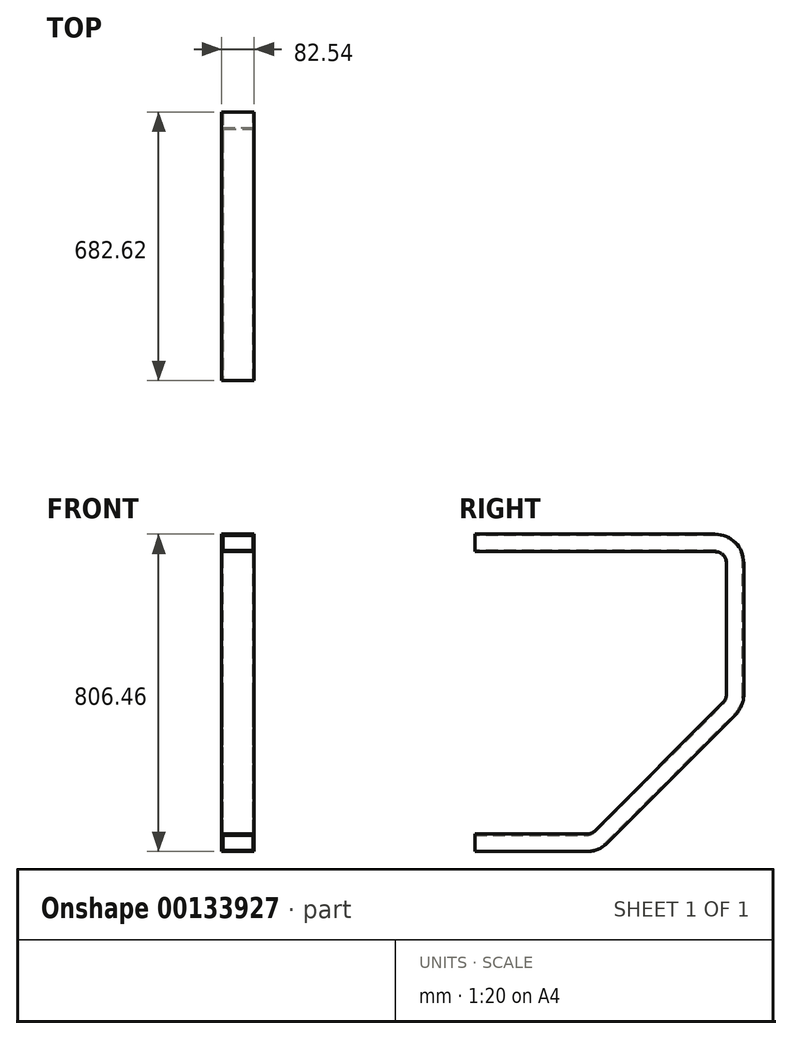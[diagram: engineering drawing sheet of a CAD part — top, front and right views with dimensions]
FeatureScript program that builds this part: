
annotation { "Feature Type Name" : "Feature", "Feature Type Description" : "" }
export const myFeature = defineFeature(function(context is Context, id is Id, definition is map)
    precondition{}
    {
        {
            var Q0;
            Q0=qCreatedBy(makeId("Right.planeOp"),FACE);
            var sketch = newSketch(context, id + "F0", { "sketchPlane" : qUnion([Q0])});
            skLineSegment(sketch, "E0", {"start": v(0, 0) * mm, "end": v(283.76, 0) * mm});
            skLineSegment(sketch, "E1", {"start": v(319.68, 14.88) * mm, "end": v(645.52, 340.72) * mm});
            skLineSegment(sketch, "E2", {"start": v(660.4, 376.64) * mm, "end": v(660.4, 711.2) * mm});
            skLineSegment(sketch, "E3", {"start": v(609.6, 762) * mm, "end": v(0, 762) * mm});
            skPoint(sketch, "E4.visualSharp", {"position": v(304.8, 0) * mm});
            skArc(sketch, "E4.filletArc", {"start": v(283.76, 0) * mm, "mid": v(303.2, 3.87) * mm, "end": v(319.68, 14.88) * mm});
            skPoint(sketch, "E5.visualSharp", {"position": v(660.4, 355.6) * mm});
            skArc(sketch, "E5.filletArc", {"start": v(645.52, 340.72) * mm, "mid": v(656.53, 357.2) * mm, "end": v(660.4, 376.64) * mm});
            skPoint(sketch, "E6.visualSharp", {"position": v(660.4, 762) * mm});
            skArc(sketch, "E6.filletArc", {"start": v(660.4, 711.2) * mm, "mid": v(645.52, 747.12) * mm, "end": v(609.6, 762) * mm});
            skSolve(sketch);
        }
        {
            var Q0;
            Q0=qCreatedBy(makeId("Front.planeOp"),FACE);
            var sketch = newSketch(context, id + "F1", { "sketchPlane" : qUnion([Q0])});
            skLineSegment(sketch, "E7.bottom", {"start": v(38.1, 19.05) * mm, "end": v(-38.1, 19.05) * mm});
            skLineSegment(sketch, "E7.top", {"start": v(38.1, -19.05) * mm, "end": v(-38.1, -19.05) * mm});
            skLineSegment(sketch, "E7.left", {"start": v(38.1, 19.05) * mm, "end": v(38.1, -19.05) * mm});
            skLineSegment(sketch, "E7.right", {"start": v(-38.1, 19.05) * mm, "end": v(-38.1, -19.05) * mm});
            skPoint(sketch, "E7.middle", {"position": v(0, 0) * mm});
            skLineSegment(sketch, "E8.0", {"start": v(41.28, 22.22) * mm, "end": v(-41.28, 22.22) * mm});
            skLineSegment(sketch, "E8.1", {"start": v(41.28, 22.22) * mm, "end": v(41.28, -22.23) * mm});
            skLineSegment(sketch, "E8.2", {"start": v(41.28, -22.23) * mm, "end": v(-41.28, -22.23) * mm});
            skLineSegment(sketch, "E8.3", {"start": v(-41.28, 22.22) * mm, "end": v(-41.28, -22.23) * mm});
            skSolve(sketch);
        }
        {
            var Q0;
            Q0=makeQuery(id+"F1.imprint","IMPRINT",FACE,{"disambiguationData":[TD([[makeQuery(id+"F1.imprint","IMPRINT",EDGE,{"derivedFrom":sQuery(id+"F1.wireOp",EDGE,"E7.bottom")}),-1.0]])]});
            var Q1;
            Q1=sQuery(id+"F0.wireOp",EDGE,"E0");
            var Q2;
            Q2=sQuery(id+"F0.wireOp",EDGE,"E4.filletArc");
            var Q3;
            Q3=sQuery(id+"F0.wireOp",EDGE,"E1");
            var Q4;
            Q4=sQuery(id+"F0.wireOp",EDGE,"E5.filletArc");
            var Q5;
            Q5=sQuery(id+"F0.wireOp",EDGE,"E2");
            var Q6;
            Q6=sQuery(id+"F0.wireOp",EDGE,"E6.filletArc");
            var Q7;
            Q7=sQuery(id+"F0.wireOp",EDGE,"E3");
            sweep(context, id + "F2", {"profiles" : qUnion([Q0]), "path" : qUnion([Q1, Q2, Q3, Q4, Q5, Q6, Q7])});
        }
    });
